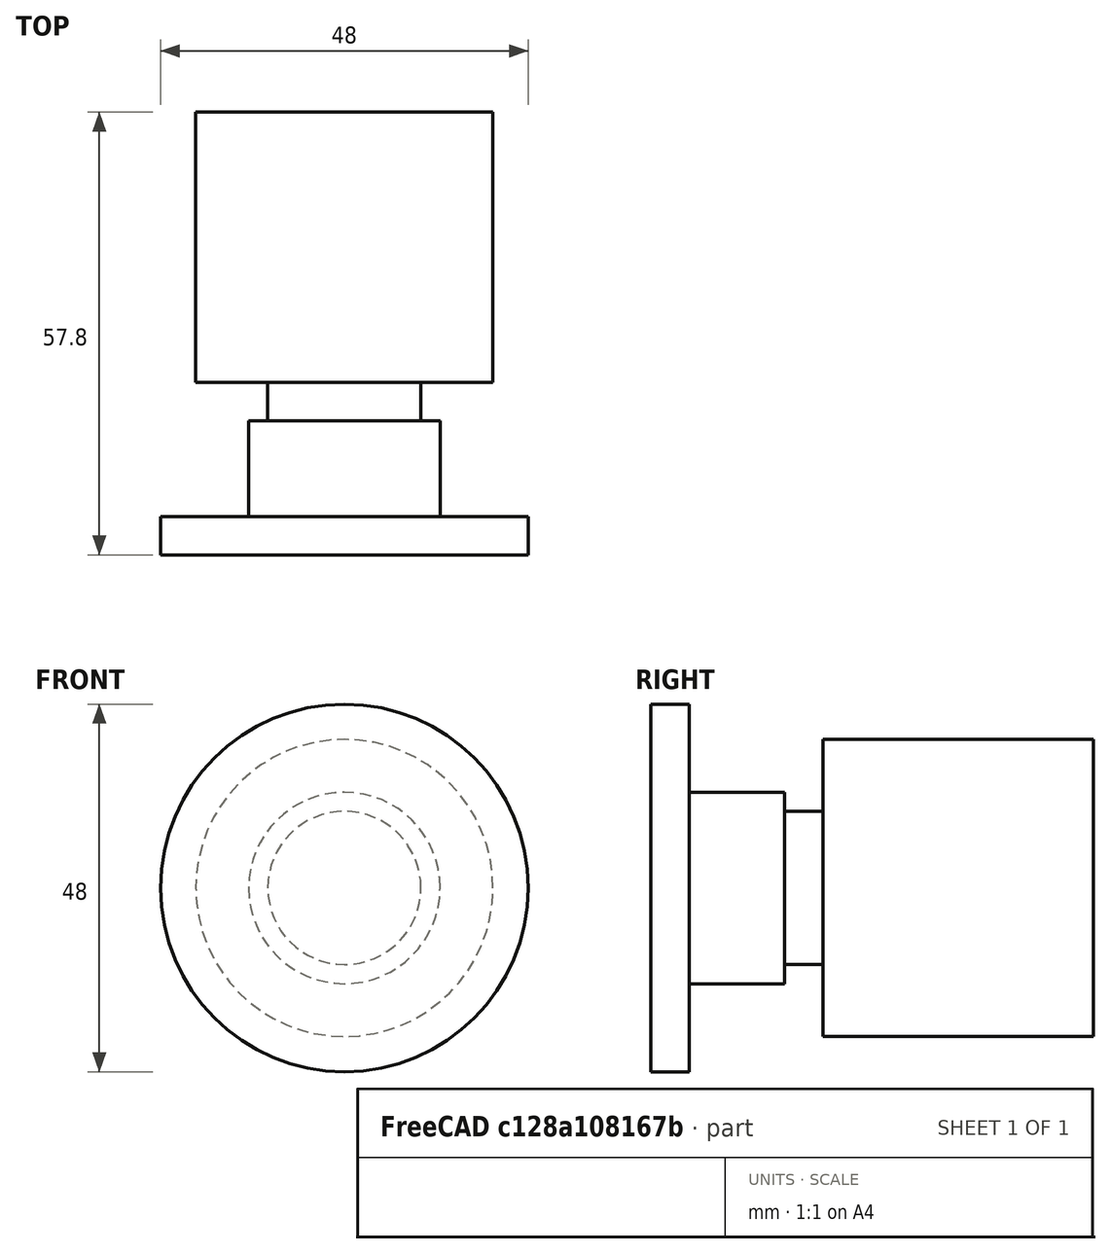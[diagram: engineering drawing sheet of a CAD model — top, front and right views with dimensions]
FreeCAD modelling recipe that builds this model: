
FCSTD DOCUMENT  (FreeCAD 0.15R4669 (Git))
Label: BR_codeur
License: All rights reserved
LicenseURL: http://en.wikipedia.org/wiki/All_rights_reserved
objects: Sketcher::SketchObject×1, Part::Revolution×1
note: 2 computed .brp shape members not serialized (recipe doc carries the construction recipe); baked Part::Feature solids carry a one-line shape summary decoded from their .brp

FEATURE [Sketcher::SketchObject] Sketch  label="coupeCodeur"
  sketch-geometry (10):
    g0: LineSegment StartX=0 StartY=28.9 StartZ=0 EndX=0 EndY=-28.9 EndZ=0
    g1: LineSegment StartX=0 StartY=28.9 StartZ=0 EndX=19.4 EndY=28.9 EndZ=0
    g2: LineSegment StartX=19.4 StartY=28.9 StartZ=0 EndX=19.4 EndY=-6.4 EndZ=0
    g3: LineSegment StartX=19.4 StartY=-6.4 StartZ=0 EndX=10 EndY=-6.4 EndZ=0
    g4: LineSegment StartX=10 StartY=-6.4 StartZ=0 EndX=10 EndY=-11.4 EndZ=0
    g5: LineSegment StartX=10 StartY=-11.4 StartZ=0 EndX=12.5 EndY=-11.4 EndZ=0
    g6: LineSegment StartX=12.5 StartY=-11.4 StartZ=0 EndX=12.5 EndY=-23.9 EndZ=0
    g7: LineSegment StartX=12.5 StartY=-23.9 StartZ=0 EndX=24 EndY=-23.9 EndZ=0
    g8: LineSegment StartX=24 StartY=-23.9 StartZ=0 EndX=24 EndY=-28.9 EndZ=0
    g9: LineSegment StartX=24 StartY=-28.9 StartZ=0 EndX=0 EndY=-28.9 EndZ=0
  constraints (30):
    c: Vertical(g0)
    c: Coincident(g0,g1)
    c: Horizontal(g1)
    c: Coincident(g1,g2)
    c: Vertical(g2)
    c: Coincident(g2,g3)
    c: Horizontal(g3)
    c: Coincident(g3,g4)
    c: Vertical(g4)
    c: Coincident(g4,g5)
    c: Coincident(g5,g6)
    c: Coincident(g6,g7)
    c: Horizontal(g7)
    c: Coincident(g7,g8)
    c: Vertical(g8)
    c: Coincident(g8,g9)
    c: Coincident(g9,g0)
    c: Horizontal(g9)
    c: Symmetric(g0,g0,g-1)
    c: PointOnObject(g0,g-2)
    c: DistanceX(g1) = 19.4
    c: DistanceX(g3,g0) = -10
    c: DistanceX(g-1,g5) = 12.5
    c: Vertical(g6)
    c: Horizontal(g5)
    c: DistanceX(g9) = -24
    c: DistanceY(g8) = -5
    c: DistanceY(g6) = -12.5
    c: DistanceY(g4) = -5
    c: DistanceY(g2) = -35.3
FEATURE [Part::Revolution] Revolve  label="codeur"
  Angle = 360
  Axis = (0,1,0)
  Base = (0,0,0)
  Solid = true
  Source = -> Sketch
